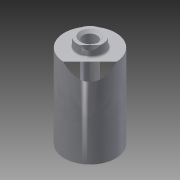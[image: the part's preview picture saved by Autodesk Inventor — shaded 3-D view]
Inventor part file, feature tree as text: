
AUTODESK INVENTOR PART (.ipt)
format: ipt  version: 2016 (Build 200138000, 138)  size: 142,848 bytes
history: native  units: mm
features: extrude x7, sketch x7, chamfer x2, fillet x1, reference x1
ambient origin geometry x8: Origin, YZ Plane, XZ Plane, XY Plane, X Axis, Y Axis, Z Axis, Center Point
bodies: Solid1 (feature_tree)
feature tree (18):
  extrude  "Extrusion1"  Depth=4.0mm
  extrude  "Extrusion2"  Depth=1.5mm
  extrude  "Extrusion3"  Depth=0.5mm TaperAngle=0.0deg
  extrude  "Extrusion4"  Depth=1.0mm TaperAngle=0.0deg
  extrude  "Extrusion5"  Depth=2.0mm
  extrude  "Extrusion6"  Depth=0.3mm
  chamfer  "Chamfer2"  Distance=2.0mm Angle=45.0deg
  extrude  "Extrusion7"  [1 undecoded]
  fillet  "Fillet1"  [1 undecoded]
  chamfer  "Chamfer3"  [1 undecoded]
  sketch  "Sketch1"  dims[d0=13.0mm d1=0.0mm d5=4.0mm]
  reference  "Reference1"
  sketch  "Sketch2"  dims[d6=1.5mm d7=0.0mm d8=2.1mm]
  sketch  "Sketch3"  dims[d9=20.0mm d10=0.0mm d11=0.5mm d12=0.0mm]
  sketch  "Sketch4"  dims[d13=0.5mm d14=0.0mm d15=1.0mm d16=0.0mm]
  sketch  "Sketch5"  dims[d17=0.2mm d18=2.0mm d19=45.0deg d20=2.2mm]
  sketch  "Sketch6"  dims[d21=30.0mm d22=0.0mm d23=0.3mm d24=0.4mm d25=2.0mm d26=45.0deg]
  sketch  "Sketch7"
note: 3 required parameter values undecoded (feature->parameter linkage not recoverable at this tier; creation-order binding heuristic only, values carry confidence <= 0.55)
